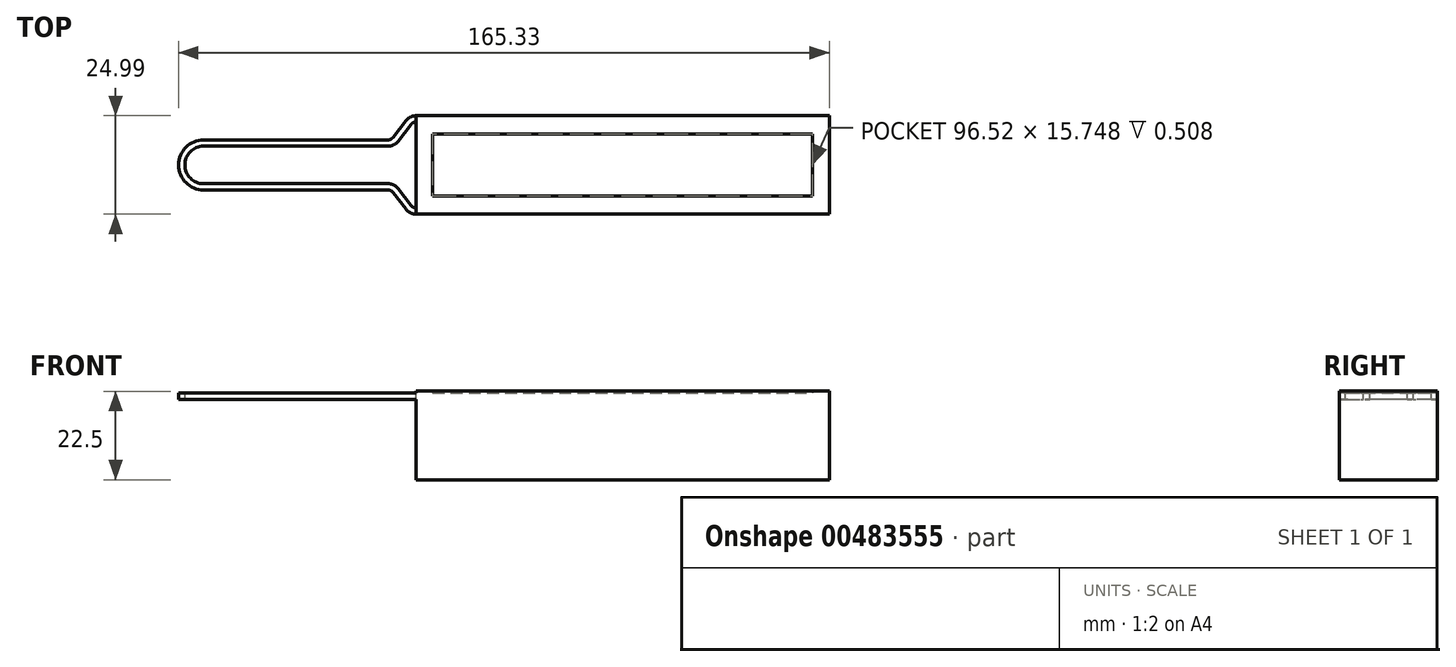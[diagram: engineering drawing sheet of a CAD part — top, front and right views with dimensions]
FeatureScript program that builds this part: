
annotation { "Feature Type Name" : "Feature", "Feature Type Description" : "" }
export const myFeature = defineFeature(function(context is Context, id is Id, definition is map)
    precondition{}
    {
        {
            var Q0;
            Q0=qCreatedBy(makeId("Top.planeOp"),FACE);
            var sketch = newSketch(context, id + "F0", { "sketchPlane" : qUnion([Q0])});
            skLineSegment(sketch, "E0.bottom", {"start": v(0, 0) * mm, "end": v(-105, 0) * mm});
            skLineSegment(sketch, "E0.top", {"start": v(0, 25) * mm, "end": v(-105, 25) * mm});
            skLineSegment(sketch, "E0.left", {"start": v(0, 0) * mm, "end": v(0, 25) * mm});
            skLineSegment(sketch, "E0.right", {"start": v(-105, 0) * mm, "end": v(-105, 25) * mm});
            skSolve(sketch);
        }
        {
            var Q0;
            Q0 = qSketchRegion(id + "F0", true);
            extrude(context, id + "F1", {"entities" : qUnion([Q0]), "depth" : 22 * mm});
        }
        {
            var Q0;
            Q0=makeQuery(id+"F1.opExtrude","CAP_FACE",FACE,{"disambiguationData":[OSD([sQuery(id+"F0.wireOp",EDGE,"E0.bottom"),sQuery(id+"F0.wireOp",EDGE,"E0.top"),sQuery(id+"F0.wireOp",EDGE,"E0.left"),sQuery(id+"F0.wireOp",EDGE,"E0.right")])],"isStart":false});
            var sketch = newSketch(context, id + "F2", { "sketchPlane" : qUnion([Q0])});
            skArc(sketch, "E1", {"start": v(-158.98, 18.85) * mm, "mid": v(-165.33, 12.5) * mm, "end": v(-158.98, 6.15) * mm});
            skArc(sketch, "E2", {"start": v(-158.98, 17.26) * mm, "mid": v(-163.74, 12.5) * mm, "end": v(-158.98, 7.73) * mm});
            skLineSegment(sketch, "E3", {"start": v(-105, 25) * mm, "end": v(-106.6, 25) * mm});
            skLineSegment(sketch, "E4", {"start": v(-106.6, 25) * mm, "end": v(-111.35, 18.85) * mm});
            skLineSegment(sketch, "E5", {"start": v(-111.35, 18.85) * mm, "end": v(-158.98, 18.85) * mm});
            skLineSegment(sketch, "E6", {"start": v(-105, 0) * mm, "end": v(-106.6, 0) * mm});
            skLineSegment(sketch, "E7", {"start": v(-106.6, 0) * mm, "end": v(-111.35, 6.15) * mm});
            skLineSegment(sketch, "E8", {"start": v(-111.35, 6.15) * mm, "end": v(-158.98, 6.15) * mm});
            skLineSegment(sketch, "E9", {"start": v(-158.98, 17.26) * mm, "end": v(-110.58, 17.26) * mm});
            skLineSegment(sketch, "E10", {"start": v(-158.98, 7.73) * mm, "end": v(-110.58, 7.73) * mm});
            skLineSegment(sketch, "E11", {"start": v(-105, 23.4) * mm, "end": v(-105.81, 23.4) * mm});
            skLineSegment(sketch, "E12", {"start": v(-105.81, 23.4) * mm, "end": v(-110.58, 17.26) * mm});
            skLineSegment(sketch, "E13", {"start": v(-105, 1.59) * mm, "end": v(-105.81, 1.59) * mm});
            skLineSegment(sketch, "E14", {"start": v(-105.81, 1.59) * mm, "end": v(-110.58, 7.73) * mm});
            skLineSegment(sketch, "E15", {"start": v(-105, 23.4) * mm, "end": v(-105, 25) * mm});
            skLineSegment(sketch, "E16", {"start": v(-105, 0) * mm, "end": v(-105, 1.59) * mm});
            skPoint(sketch, "E17.orphan", {"position": v(-158.98, 6.15) * mm});
            skSolve(sketch);
        }
        {
            var Q0;
            Q0 = qSketchRegion(id + "F2", true);
            extrude(context, id + "F3", {"entities" : qUnion([Q0]), "operationType" : NewBodyOperationType.ADD, "oppositeDirection" : true, "depth" : 1.59 * mm});
        }
        {
            var Q0;
            Q0=makeQuery(id+"F3.opExtrude","SWEPT_EDGE",EDGE,{"disambiguationData":[OSD([sQuery(id+"F2.wireOp",EDGE,"E4"),sQuery(id+"F2.wireOp",EDGE,"E5")])]});
            var Q1;
            Q1=makeQuery(id+"F3.opExtrude","SWEPT_EDGE",EDGE,{"disambiguationData":[OSD([sQuery(id+"F2.wireOp",EDGE,"E11"),sQuery(id+"F2.wireOp",EDGE,"E12")])]});
            var Q2;
            Q2=makeQuery(id+"F3.opExtrude","SWEPT_EDGE",EDGE,{"disambiguationData":[OSD([sQuery(id+"F2.wireOp",EDGE,"E7"),sQuery(id+"F2.wireOp",EDGE,"E8")])]});
            var Q3;
            Q3=makeQuery(id+"F3.opExtrude","SWEPT_EDGE",EDGE,{"disambiguationData":[OSD([sQuery(id+"F2.wireOp",EDGE,"E13"),sQuery(id+"F2.wireOp",EDGE,"E14")])]});
            fillet(context, id + "F4", {"entities" : qUnion([Q0, Q1, Q2, Q3]), "radius" : 1.59 * mm, "tangentPropagation" : true, "allowEdgeOverflow" : false});
        }
        {
            var Q0;
            Q0=makeQuery(id+"F3.opExtrude","SWEPT_EDGE",EDGE,{"disambiguationData":[OSD([sQuery(id+"F2.wireOp",EDGE,"E10"),sQuery(id+"F2.wireOp",EDGE,"E14")])]});
            var Q1;
            Q1=makeQuery(id+"F3.opExtrude","SWEPT_EDGE",EDGE,{"disambiguationData":[OSD([sQuery(id+"F2.wireOp",EDGE,"E3"),sQuery(id+"F2.wireOp",EDGE,"E4")])]});
            var Q2;
            Q2=makeQuery(id+"F3.opExtrude","SWEPT_EDGE",EDGE,{"disambiguationData":[OSD([sQuery(id+"F2.wireOp",EDGE,"E9"),sQuery(id+"F2.wireOp",EDGE,"E12")])]});
            var Q3;
            Q3=makeQuery(id+"F3.opExtrude","SWEPT_EDGE",EDGE,{"disambiguationData":[OSD([sQuery(id+"F2.wireOp",EDGE,"E6"),sQuery(id+"F2.wireOp",EDGE,"E7")])]});
            fillet(context, id + "F5", {"entities" : qUnion([Q0, Q1, Q2, Q3]), "radius" : 3.17 * mm, "tangentPropagation" : true, "allowEdgeOverflow" : false});
        }
        {
            var Q0;
            Q0=makeQuery(id+"F3.boolean.opBoolean","MERGE",FACE,{"derivedFrom":[makeQuery(id+"F1.opExtrude","CAP_FACE",FACE,{"disambiguationData":[OSD([sQuery(id+"F0.wireOp",EDGE,"E0.bottom"),sQuery(id+"F0.wireOp",EDGE,"E0.top"),sQuery(id+"F0.wireOp",EDGE,"E0.left"),sQuery(id+"F0.wireOp",EDGE,"E0.right")])],"isStart":false}),makeQuery(id+"F3.opExtrude","CAP_FACE",FACE,{"disambiguationData":[OSD([sQuery(id+"F2.wireOp",EDGE,"E1"),sQuery(id+"F2.wireOp",EDGE,"E2"),sQuery(id+"F2.wireOp",EDGE,"E3"),sQuery(id+"F2.wireOp",EDGE,"E4"),sQuery(id+"F2.wireOp",EDGE,"E5"),sQuery(id+"F2.wireOp",EDGE,"E6"),sQuery(id+"F2.wireOp",EDGE,"E7"),sQuery(id+"F2.wireOp",EDGE,"E8"),sQuery(id+"F2.wireOp",EDGE,"E9"),sQuery(id+"F2.wireOp",EDGE,"E10"),sQuery(id+"F2.wireOp",EDGE,"E11"),sQuery(id+"F2.wireOp",EDGE,"E12"),sQuery(id+"F2.wireOp",EDGE,"E13"),sQuery(id+"F2.wireOp",EDGE,"E14"),sQuery(id+"F2.wireOp",EDGE,"E15"),sQuery(id+"F2.wireOp",EDGE,"E16")])],"isStart":true})]});
            var sketch = newSketch(context, id + "F6", { "sketchPlane" : qUnion([Q0])});
            skLineSegment(sketch, "E18", {"start": v(0, 0) * mm, "end": v(0, 25) * mm});
            skLineSegment(sketch, "E19", {"start": v(0, 25) * mm, "end": v(-105.03, 25) * mm});
            skLineSegment(sketch, "E20", {"start": v(-105.03, 25) * mm, "end": v(-105.03, 0) * mm});
            skLineSegment(sketch, "E21", {"start": v(-105.03, 0) * mm, "end": v(0, 0) * mm});
            skLineSegment(sketch, "E22.bottom", {"start": v(-100.78, 20.37) * mm, "end": v(-4.26, 20.37) * mm});
            skLineSegment(sketch, "E22.top", {"start": v(-100.78, 4.62) * mm, "end": v(-4.26, 4.62) * mm});
            skLineSegment(sketch, "E22.left", {"start": v(-100.78, 20.37) * mm, "end": v(-100.78, 4.62) * mm});
            skLineSegment(sketch, "E22.right", {"start": v(-4.26, 20.37) * mm, "end": v(-4.26, 4.62) * mm});
            skSolve(sketch);
        }
        {
            var Q0;
            Q0 = qSketchRegion(id + "F6", true);
            extrude(context, id + "F7", {"entities" : qUnion([Q0]), "operationType" : NewBodyOperationType.ADD, "depth" : 0.5 * mm, "offsetDistance" : 25.4 * mm});
        }
    });
